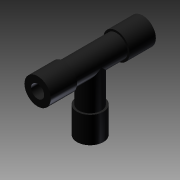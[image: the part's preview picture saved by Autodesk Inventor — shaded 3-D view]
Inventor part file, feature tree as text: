
AUTODESK INVENTOR PART (.ipt)
format: ipt  version: 2011 (Build 150239000, 239)  size: 145,408 bytes
history: native  units: in
note: dims shown in document units (in); Inventor stores cm internally (conversion verified against a paired STEP export)
features: extrude x6, sketch x6, plane x2, projected_geometry x1
ambient origin geometry x8: Origin, YZ Plane, XZ Plane, XY Plane, X Axis, Y Axis, Z Axis, Center Point
bodies: Solid1 (feature_tree)
feature tree (15):
  extrude  "Extrusion1"  Depth=0.25in
  extrude  "Extrusion2"  Depth=0.425in
  extrude  "Extrusion3"  Depth=0.5in
  plane  "Work Plane3"
  extrude  "Extrusion4"  Depth=0.775in
  extrude  "Extrusion5"  Depth=0.925in TaperAngle=0.0deg
  plane  "Work Plane5"
  extrude  "Extrusion7"  Depth=0.5in TaperAngle=0.0deg
  sketch  "Sketch1"  dims[d0=0.5in d1=0.25in]
  sketch  "Sketch2"  dims[d2=0.5in d3=0.0in d4=0.425in]
  sketch  "Sketch3"  dims[d5=1.0in d6=0.0in d7=0.5in]
  sketch  "Sketch4"  dims[d8=0.5in d9=0.0in d12=0.775in]
  projected_geometry  "Projected Loop1"
  sketch  "Sketch5"  dims[d13=0.25in d14=0.925in d15=0.0in]
  sketch  "Sketch7"  dims[d16=0.5in d17=0.5in d18=0.0in d20=0.0in d23=1.0in d24=0.0in]
